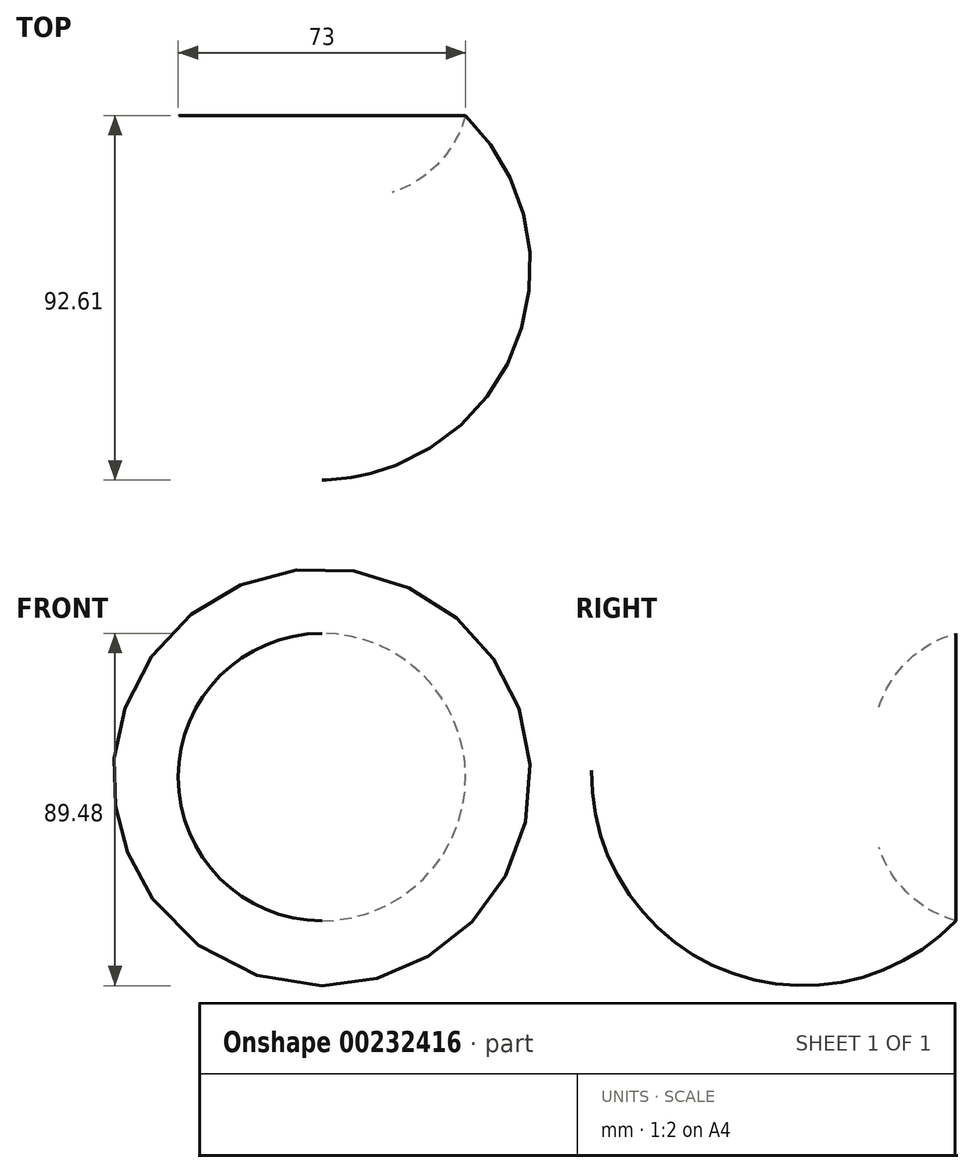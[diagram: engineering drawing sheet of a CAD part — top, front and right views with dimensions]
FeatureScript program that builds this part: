
annotation { "Feature Type Name" : "Feature", "Feature Type Description" : "" }
export const myFeature = defineFeature(function(context is Context, id is Id, definition is map)
    precondition{}
    {
        {
            var Q0;
            Q0=qCreatedBy(makeId("Top.planeOp"),FACE);
            var sketch = newSketch(context, id + "F0", { "sketchPlane" : qUnion([Q0])});
            skLineSegment(sketch, "E0", {"start": v(0, 76.76) * mm, "end": v(0, -93.98) * mm});
            skArc(sketch, "E1", {"start": v(0, -50.62) * mm, "mid": v(52.98, 3.22) * mm, "end": v(0, 57.05) * mm});
            skArc(sketch, "E2", {"start": v(0, 22.4) * mm, "mid": v(37.53, 49.58) * mm, "end": v(0, 76.76) * mm});
            skSolve(sketch);
        }
        {
            var Q0;
            Q0 = qSketchRegion(id + "F0", true);
            var Q1;
            Q1=sQuery(id+"F0.wireOp",EDGE,"E0");
            revolve(context, id + "F1", {"entities" : qUnion([Q0]), "axis" : qUnion([Q1]), "revolveType" : RevolveType.FULL});
        }
    });
